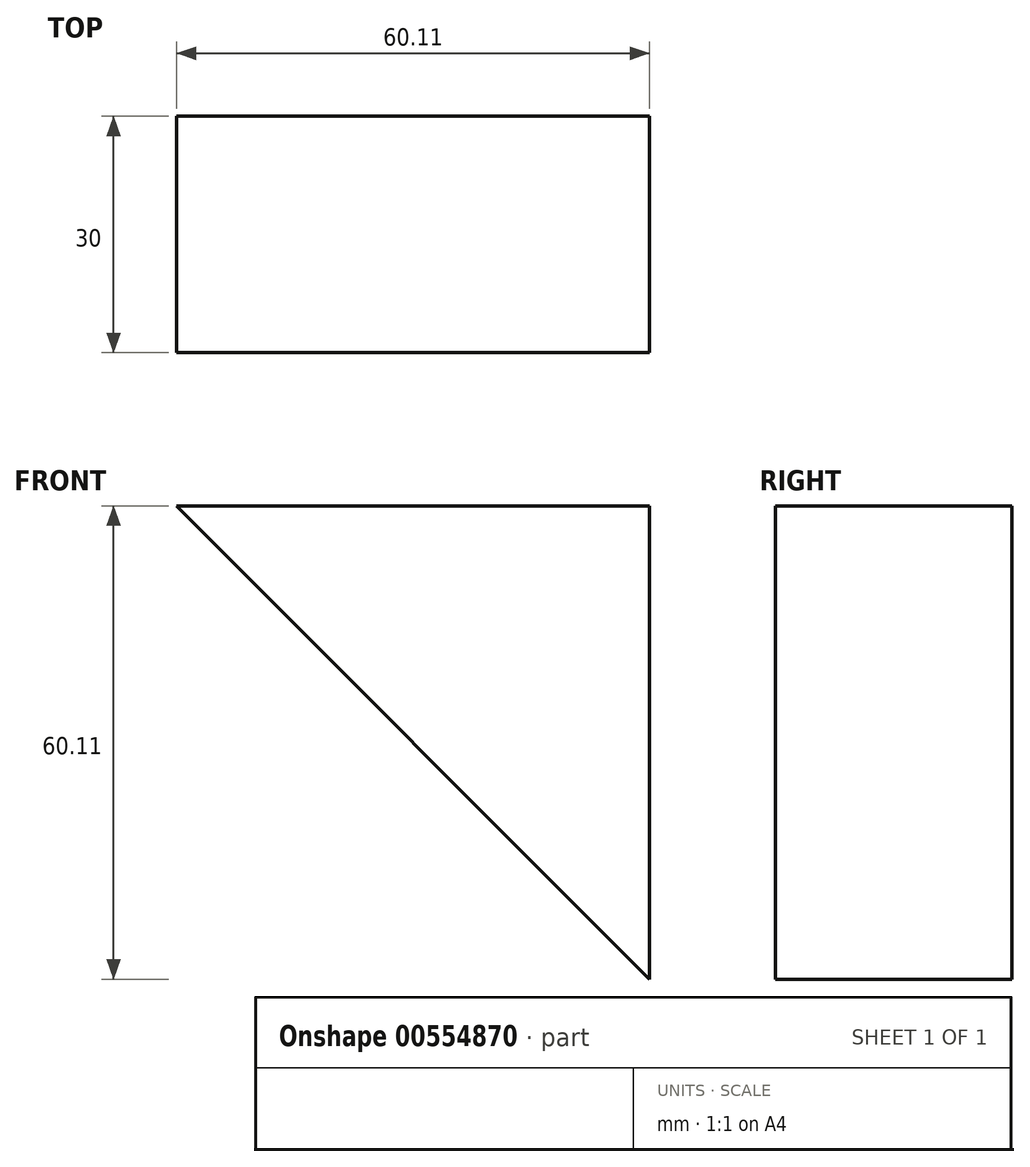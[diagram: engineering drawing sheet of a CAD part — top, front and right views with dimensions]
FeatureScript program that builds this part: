
annotation { "Feature Type Name" : "Feature", "Feature Type Description" : "" }
export const myFeature = defineFeature(function(context is Context, id is Id, definition is map)
    precondition{}
    {
        {
            var Q0;
            Q0=qCreatedBy(makeId("Front.planeOp"),FACE);
            var sketch = newSketch(context, id + "F0", { "sketchPlane" : qUnion([Q0])});
            skLineSegment(sketch, "E0", {"start": v(-71.77, 33.68) * mm, "end": v(-11.66, -26.43) * mm});
            skLineSegment(sketch, "E1", {"start": v(-71.77, 33.68) * mm, "end": v(-11.66, 33.68) * mm});
            skLineSegment(sketch, "E2", {"start": v(-11.66, 33.68) * mm, "end": v(-11.66, -26.43) * mm});
            skSolve(sketch);
        }
        {
            var Q0;
            Q0 = qSketchRegion(id + "F0", true);
            extrude(context, id + "F1", {"entities" : qUnion([Q0]), "depth" : 30 * mm, "offsetDistance" : 25 * mm});
        }
    });
